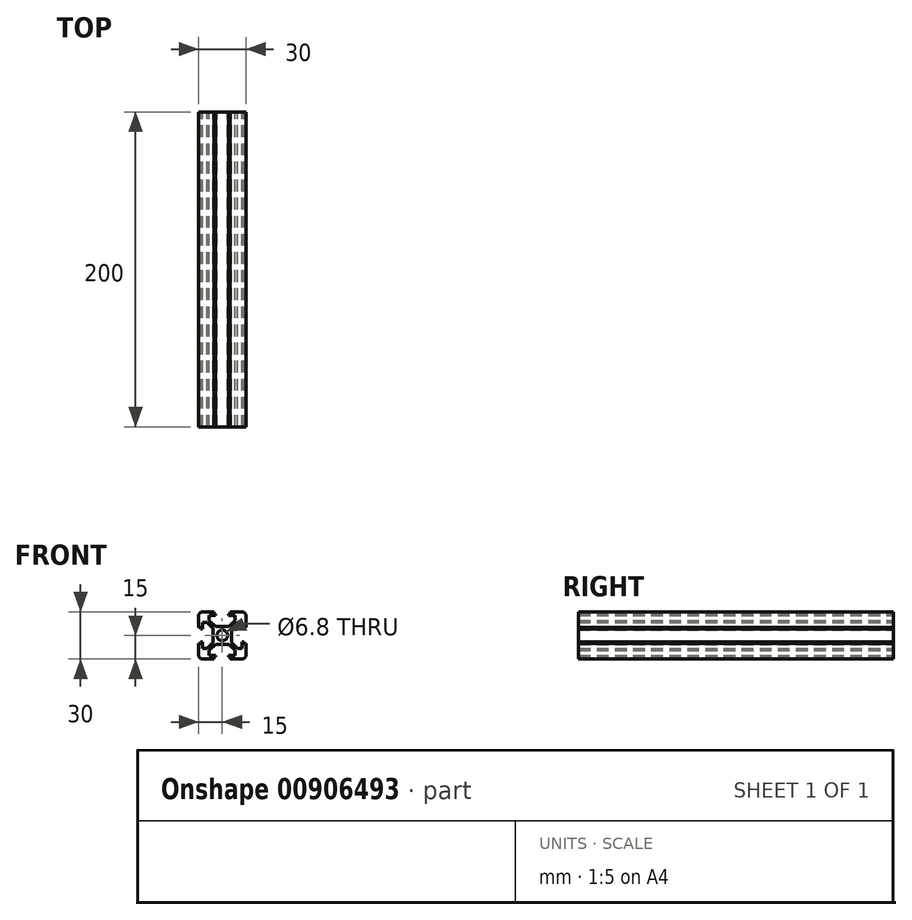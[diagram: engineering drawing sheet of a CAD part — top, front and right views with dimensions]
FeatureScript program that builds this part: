
annotation { "Feature Type Name" : "Feature", "Feature Type Description" : "" }
export const myFeature = defineFeature(function(context is Context, id is Id, definition is map)
    precondition{}
    {
        {
            var Q0;
            Q0=qCreatedBy(makeId("Front.planeOp"),FACE);
            var sketch = newSketch(context, id + "F0", { "sketchPlane" : qUnion([Q0])});
            skArc(sketch, "E0", {"start": v(0, 3.4) * mm, "mid": v(2.4, 2.4) * mm, "end": v(3.4, 0) * mm});
            skPoint(sketch, "E1", {"position": v(15, 0) * mm});
            skPoint(sketch, "E2", {"position": v(5.8, 0) * mm});
            skPoint(sketch, "E3", {"position": v(0, 15) * mm});
            skPoint(sketch, "E4", {"position": v(0, 5.8) * mm});
            skPoint(sketch, "E5", {"position": v(8.25, 8.25) * mm});
            skPoint(sketch, "E6", {"position": v(15, 5.1) * mm});
            skPoint(sketch, "E7", {"position": v(12.6, 0) * mm});
            skPoint(sketch, "E8", {"position": v(0, 12.6) * mm});
            skPoint(sketch, "E9", {"position": v(5.1, 15) * mm});
            skPoint(sketch, "E10", {"position": v(4.1, 12.6) * mm});
            skPoint(sketch, "E11", {"position": v(12.6, 4.1) * mm});
            skLineSegment(sketch, "E12", {"start": v(5.1, 15) * mm, "end": v(12.5, 15) * mm});
            skLineSegment(sketch, "E13", {"start": v(15, 12.5) * mm, "end": v(15, 5.1) * mm});
            skPoint(sketch, "E14.visualSharp", {"position": v(15, 15) * mm});
            skArc(sketch, "E14.filletArc", {"start": v(15, 12.5) * mm, "mid": v(14.27, 14.27) * mm, "end": v(12.5, 15) * mm});
            skPoint(sketch, "E15", {"position": v(8.25, 12.6) * mm});
            skPoint(sketch, "E16", {"position": v(12.6, 8.25) * mm});
            skLineSegment(sketch, "E17", {"start": v(12.6, 4.1) * mm, "end": v(12.6, 8.25) * mm});
            skLineSegment(sketch, "E18", {"start": v(4.1, 12.6) * mm, "end": v(8.25, 12.6) * mm});
            skPoint(sketch, "E19", {"position": v(5.8, 5.8) * mm});
            skLineSegment(sketch, "E20", {"start": v(0, 5.8) * mm, "end": v(4.39, 5.8) * mm});
            skLineSegment(sketch, "E21", {"start": v(5.8, 0) * mm, "end": v(5.8, 4.39) * mm});
            skLineSegment(sketch, "E22", {"start": v(5.1, 6.5) * mm, "end": v(8.25, 9.66) * mm});
            skLineSegment(sketch, "E23", {"start": v(6.5, 5.1) * mm, "end": v(9.66, 8.25) * mm});
            skLineSegment(sketch, "E24", {"start": v(6.5, 5.1) * mm, "end": v(5.8, 4.39) * mm});
            skLineSegment(sketch, "E25", {"start": v(5.1, 6.5) * mm, "end": v(4.39, 5.8) * mm});
            skLineSegment(sketch, "E26", {"start": v(12.6, 8.25) * mm, "end": v(9.66, 8.25) * mm});
            skLineSegment(sketch, "E27", {"start": v(8.25, 12.6) * mm, "end": v(8.25, 9.66) * mm});
            skPoint(sketch, "E28", {"position": v(8.25, 9.66) * mm});
            skPoint(sketch, "E29", {"position": v(9.66, 8.25) * mm});
            skPoint(sketch, "E30", {"position": v(13.8, 5.1) * mm});
            skPoint(sketch, "E31", {"position": v(13.8, 4.1) * mm});
            skLineSegment(sketch, "E32", {"start": v(12.6, 4.1) * mm, "end": v(13.8, 4.1) * mm});
            skLineSegment(sketch, "E33", {"start": v(13.8, 5.1) * mm, "end": v(13.8, 4.1) * mm});
            skLineSegment(sketch, "E34", {"start": v(13.8, 5.1) * mm, "end": v(15, 5.1) * mm});
            skPoint(sketch, "E35", {"position": v(5.1, 13.8) * mm});
            skLineSegment(sketch, "E36", {"start": v(5.1, 15) * mm, "end": v(5.1, 13.8) * mm});
            skLineSegment(sketch, "E37", {"start": v(4.1, 13.8) * mm, "end": v(4.1, 12.6) * mm});
            skLineSegment(sketch, "E38", {"start": v(4.1, 13.8) * mm, "end": v(5.1, 13.8) * mm});
            skLineSegment(sketch, "E39.1.0", {"start": v(-5.1, 6.5) * mm, "end": v(-8.25, 9.66) * mm});
            skLineSegment(sketch, "E39.1.2", {"start": v(-6.5, 5.1) * mm, "end": v(-9.66, 8.25) * mm});
            skPoint(sketch, "E39.1.3", {"position": v(-4.1, 12.6) * mm});
            skLineSegment(sketch, "E39.1.4", {"start": v(-15, 5.1) * mm, "end": v(-15, 12.5) * mm});
            skPoint(sketch, "E39.1.6", {"position": v(-15, 15) * mm});
            skPoint(sketch, "E39.1.7", {"position": v(-8.25, 8.25) * mm});
            skLineSegment(sketch, "E39.1.8", {"start": v(-5.8, 0) * mm, "end": v(-5.8, 4.39) * mm});
            skPoint(sketch, "E39.1.9", {"position": v(-8.25, 12.6) * mm});
            skLineSegment(sketch, "E39.1.10", {"start": v(-12.5, 15) * mm, "end": v(-5.1, 15) * mm});
            skPoint(sketch, "E39.1.11", {"position": v(-5.8, 0) * mm});
            skPoint(sketch, "E39.1.12", {"position": v(-12.6, 8.25) * mm});
            skLineSegment(sketch, "E39.1.13", {"start": v(0, 5.8) * mm, "end": v(-4.39, 5.8) * mm});
            skPoint(sketch, "E39.1.14", {"position": v(-12.6, 0) * mm});
            skPoint(sketch, "E39.1.15", {"position": v(-15, 5.1) * mm});
            skLineSegment(sketch, "E39.1.16", {"start": v(-12.6, 8.25) * mm, "end": v(-9.66, 8.25) * mm});
            skPoint(sketch, "E39.1.17", {"position": v(-5.8, 5.8) * mm});
            skLineSegment(sketch, "E39.1.18", {"start": v(-12.6, 4.1) * mm, "end": v(-12.6, 8.25) * mm});
            skPoint(sketch, "E39.1.19", {"position": v(-9.66, 8.25) * mm});
            skPoint(sketch, "E39.1.20", {"position": v(-5.1, 15) * mm});
            skArc(sketch, "E39.1.21", {"start": v(-3.4, 0) * mm, "mid": v(-2.4, 2.4) * mm, "end": v(0, 3.4) * mm});
            skPoint(sketch, "E39.1.22", {"position": v(-13.8, 5.1) * mm});
            skPoint(sketch, "E39.1.23", {"position": v(-12.6, 4.1) * mm});
            skPoint(sketch, "E39.1.25", {"position": v(-4.1, 13.8) * mm});
            skPoint(sketch, "E39.1.26", {"position": v(-15, 0) * mm});
            skArc(sketch, "E39.1.27", {"start": v(-12.5, 15) * mm, "mid": v(-14.27, 14.27) * mm, "end": v(-15, 12.5) * mm});
            skPoint(sketch, "E39.1.28", {"position": v(-8.25, 9.66) * mm});
            skLineSegment(sketch, "E39.1.29", {"start": v(-4.1, 12.6) * mm, "end": v(-8.25, 12.6) * mm});
            skLineSegment(sketch, "E39.1.30", {"start": v(-8.25, 12.6) * mm, "end": v(-8.25, 9.66) * mm});
            skPoint(sketch, "E39.1.31", {"position": v(-5.1, 13.8) * mm});
            skLineSegment(sketch, "E39.1.33", {"start": v(-13.8, 4.1) * mm, "end": v(-13.8, 5.1) * mm});
            skLineSegment(sketch, "E39.1.34", {"start": v(-6.5, 5.1) * mm, "end": v(-5.8, 4.39) * mm});
            skLineSegment(sketch, "E39.1.35", {"start": v(-5.1, 6.5) * mm, "end": v(-4.39, 5.8) * mm});
            skLineSegment(sketch, "E39.1.36", {"start": v(-13.8, 4.1) * mm, "end": v(-12.6, 4.1) * mm});
            skLineSegment(sketch, "E39.1.37", {"start": v(-4.1, 12.6) * mm, "end": v(-4.1, 13.8) * mm});
            skLineSegment(sketch, "E39.1.38", {"start": v(-5.1, 13.8) * mm, "end": v(-4.1, 13.8) * mm});
            skLineSegment(sketch, "E39.1.39", {"start": v(-5.1, 13.8) * mm, "end": v(-5.1, 15) * mm});
            skLineSegment(sketch, "E39.1.40", {"start": v(-15, 5.1) * mm, "end": v(-13.8, 5.1) * mm});
            skLineSegment(sketch, "E39.2.0", {"start": v(-6.5, -5.1) * mm, "end": v(-9.66, -8.25) * mm});
            skPoint(sketch, "E39.2.1", {"position": v(-5.8, 0) * mm});
            skLineSegment(sketch, "E39.2.2", {"start": v(-5.1, -6.5) * mm, "end": v(-8.25, -9.66) * mm});
            skPoint(sketch, "E39.2.3", {"position": v(-12.6, -4.1) * mm});
            skLineSegment(sketch, "E39.2.4", {"start": v(-5.1, -15) * mm, "end": v(-12.5, -15) * mm});
            skPoint(sketch, "E39.2.5", {"position": v(-12.6, 0) * mm});
            skPoint(sketch, "E39.2.6", {"position": v(-15, -15) * mm});
            skPoint(sketch, "E39.2.7", {"position": v(-8.25, -8.25) * mm});
            skLineSegment(sketch, "E39.2.8", {"start": v(0, -5.8) * mm, "end": v(-4.39, -5.8) * mm});
            skPoint(sketch, "E39.2.9", {"position": v(-12.6, -8.25) * mm});
            skLineSegment(sketch, "E39.2.10", {"start": v(-15, -12.5) * mm, "end": v(-15, -5.1) * mm});
            skPoint(sketch, "E39.2.11", {"position": v(0, -5.8) * mm});
            skPoint(sketch, "E39.2.12", {"position": v(-8.25, -12.6) * mm});
            skLineSegment(sketch, "E39.2.13", {"start": v(-5.8, 0) * mm, "end": v(-5.8, -4.39) * mm});
            skPoint(sketch, "E39.2.14", {"position": v(0, -12.6) * mm});
            skPoint(sketch, "E39.2.15", {"position": v(-5.1, -15) * mm});
            skLineSegment(sketch, "E39.2.16", {"start": v(-8.25, -12.6) * mm, "end": v(-8.25, -9.66) * mm});
            skPoint(sketch, "E39.2.17", {"position": v(-5.8, -5.8) * mm});
            skLineSegment(sketch, "E39.2.18", {"start": v(-4.1, -12.6) * mm, "end": v(-8.25, -12.6) * mm});
            skPoint(sketch, "E39.2.19", {"position": v(-8.25, -9.66) * mm});
            skPoint(sketch, "E39.2.20", {"position": v(-15, -5.1) * mm});
            skArc(sketch, "E39.2.21", {"start": v(0, -3.4) * mm, "mid": v(-2.4, -2.4) * mm, "end": v(-3.4, 0) * mm});
            skPoint(sketch, "E39.2.22", {"position": v(-5.1, -13.8) * mm});
            skPoint(sketch, "E39.2.23", {"position": v(-4.1, -12.6) * mm});
            skPoint(sketch, "E39.2.24", {"position": v(-15, 0) * mm});
            skPoint(sketch, "E39.2.25", {"position": v(-13.8, -4.1) * mm});
            skPoint(sketch, "E39.2.26", {"position": v(0, -15) * mm});
            skArc(sketch, "E39.2.27", {"start": v(-15, -12.5) * mm, "mid": v(-14.27, -14.27) * mm, "end": v(-12.5, -15) * mm});
            skPoint(sketch, "E39.2.28", {"position": v(-9.66, -8.25) * mm});
            skLineSegment(sketch, "E39.2.29", {"start": v(-12.6, -4.1) * mm, "end": v(-12.6, -8.25) * mm});
            skLineSegment(sketch, "E39.2.30", {"start": v(-12.6, -8.25) * mm, "end": v(-9.66, -8.25) * mm});
            skPoint(sketch, "E39.2.31", {"position": v(-13.8, -5.1) * mm});
            skLineSegment(sketch, "E39.2.33", {"start": v(-4.1, -13.8) * mm, "end": v(-5.1, -13.8) * mm});
            skLineSegment(sketch, "E39.2.34", {"start": v(-5.1, -6.5) * mm, "end": v(-4.39, -5.8) * mm});
            skLineSegment(sketch, "E39.2.35", {"start": v(-6.5, -5.1) * mm, "end": v(-5.8, -4.39) * mm});
            skLineSegment(sketch, "E39.2.36", {"start": v(-4.1, -13.8) * mm, "end": v(-4.1, -12.6) * mm});
            skLineSegment(sketch, "E39.2.37", {"start": v(-12.6, -4.1) * mm, "end": v(-13.8, -4.1) * mm});
            skLineSegment(sketch, "E39.2.38", {"start": v(-13.8, -5.1) * mm, "end": v(-13.8, -4.1) * mm});
            skLineSegment(sketch, "E39.2.39", {"start": v(-13.8, -5.1) * mm, "end": v(-15, -5.1) * mm});
            skLineSegment(sketch, "E39.2.40", {"start": v(-5.1, -15) * mm, "end": v(-5.1, -13.8) * mm});
            skLineSegment(sketch, "E39.3.0", {"start": v(5.1, -6.5) * mm, "end": v(8.25, -9.66) * mm});
            skPoint(sketch, "E39.3.1", {"position": v(0, -5.8) * mm});
            skLineSegment(sketch, "E39.3.2", {"start": v(6.5, -5.1) * mm, "end": v(9.66, -8.25) * mm});
            skPoint(sketch, "E39.3.3", {"position": v(4.1, -12.6) * mm});
            skLineSegment(sketch, "E39.3.4", {"start": v(15, -5.1) * mm, "end": v(15, -12.5) * mm});
            skPoint(sketch, "E39.3.5", {"position": v(0, -12.6) * mm});
            skPoint(sketch, "E39.3.6", {"position": v(15, -15) * mm});
            skPoint(sketch, "E39.3.7", {"position": v(8.25, -8.25) * mm});
            skLineSegment(sketch, "E39.3.8", {"start": v(5.8, 0) * mm, "end": v(5.8, -4.39) * mm});
            skPoint(sketch, "E39.3.9", {"position": v(8.25, -12.6) * mm});
            skLineSegment(sketch, "E39.3.10", {"start": v(12.5, -15) * mm, "end": v(5.1, -15) * mm});
            skPoint(sketch, "E39.3.12", {"position": v(12.6, -8.25) * mm});
            skLineSegment(sketch, "E39.3.13", {"start": v(0, -5.8) * mm, "end": v(4.39, -5.8) * mm});
            skPoint(sketch, "E39.3.15", {"position": v(15, -5.1) * mm});
            skLineSegment(sketch, "E39.3.16", {"start": v(12.6, -8.25) * mm, "end": v(9.66, -8.25) * mm});
            skPoint(sketch, "E39.3.17", {"position": v(5.8, -5.8) * mm});
            skLineSegment(sketch, "E39.3.18", {"start": v(12.6, -4.1) * mm, "end": v(12.6, -8.25) * mm});
            skPoint(sketch, "E39.3.19", {"position": v(9.66, -8.25) * mm});
            skPoint(sketch, "E39.3.20", {"position": v(5.1, -15) * mm});
            skArc(sketch, "E39.3.21", {"start": v(3.4, 0) * mm, "mid": v(2.4, -2.4) * mm, "end": v(0, -3.4) * mm});
            skPoint(sketch, "E39.3.22", {"position": v(13.8, -5.1) * mm});
            skPoint(sketch, "E39.3.23", {"position": v(12.6, -4.1) * mm});
            skPoint(sketch, "E39.3.24", {"position": v(0, -15) * mm});
            skPoint(sketch, "E39.3.25", {"position": v(4.1, -13.8) * mm});
            skArc(sketch, "E39.3.27", {"start": v(12.5, -15) * mm, "mid": v(14.27, -14.27) * mm, "end": v(15, -12.5) * mm});
            skPoint(sketch, "E39.3.28", {"position": v(8.25, -9.66) * mm});
            skLineSegment(sketch, "E39.3.29", {"start": v(4.1, -12.6) * mm, "end": v(8.25, -12.6) * mm});
            skLineSegment(sketch, "E39.3.30", {"start": v(8.25, -12.6) * mm, "end": v(8.25, -9.66) * mm});
            skPoint(sketch, "E39.3.31", {"position": v(5.1, -13.8) * mm});
            skLineSegment(sketch, "E39.3.33", {"start": v(13.8, -4.1) * mm, "end": v(13.8, -5.1) * mm});
            skLineSegment(sketch, "E39.3.34", {"start": v(6.5, -5.1) * mm, "end": v(5.8, -4.39) * mm});
            skLineSegment(sketch, "E39.3.35", {"start": v(5.1, -6.5) * mm, "end": v(4.39, -5.8) * mm});
            skLineSegment(sketch, "E39.3.36", {"start": v(13.8, -4.1) * mm, "end": v(12.6, -4.1) * mm});
            skLineSegment(sketch, "E39.3.37", {"start": v(4.1, -12.6) * mm, "end": v(4.1, -13.8) * mm});
            skLineSegment(sketch, "E39.3.38", {"start": v(5.1, -13.8) * mm, "end": v(4.1, -13.8) * mm});
            skLineSegment(sketch, "E39.3.39", {"start": v(5.1, -13.8) * mm, "end": v(5.1, -15) * mm});
            skLineSegment(sketch, "E39.3.40", {"start": v(15, -5.1) * mm, "end": v(13.8, -5.1) * mm});
            skSolve(sketch);
        }
        {
            var Q0;
            Q0 = qSketchRegion(id + "F0", true);
            extrude(context, id + "F1", {"entities" : qUnion([Q0]), "depth" : 200 * mm, "offsetDistance" : 25 * mm});
        }
    });
